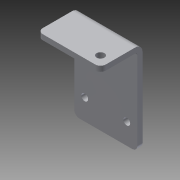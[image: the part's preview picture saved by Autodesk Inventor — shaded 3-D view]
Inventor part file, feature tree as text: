
AUTODESK INVENTOR PART (.ipt)
format: ipt  version: 2014 (Build 180170000, 170)  size: 122,368 bytes
history: native  units: in
note: dims shown in document units (in); Inventor stores cm internally (conversion verified against a paired STEP export)
features: sheet_metal_op x4, sketch x3, other x3, fillet x1
ambient origin geometry x8: Origin, YZ Plane, XZ Plane, XY Plane, X Axis, Y Axis, Z Axis, Center Point
bodies: Solid1 (feature_tree)
feature tree (11):
  sheet_metal_op  "Face1"
  sheet_metal_op  "Flange1"
  fillet  "Fillet1"  Radius=1.5in
  sketch  "Sketch1"  dims[d1=2.0in]
  other  "Plate1"
  sketch  "Sketch2"  dims[d2=0.163in]
  other  "Plate2"
  sheet_metal_op  "Bend1"
  sheet_metal_op  "Corner1"
  sketch  "Sketch4"  dims[d3=0.25in d4=0.7874in d6=1.0in d7=0.3937in d9=1.0in d11=0.125in d12=0.125in d13=0.0625in d14=0.25in d15=0.125in d16=1.0in d17=90.0deg d18=0.05in d19=0.5in d20=0.125in d21=0.125in d22=0.5in d28=0.187in d29=0.25in d30=0.25in d31=0.125in d32=0.0in d33=0.125in]
  other  "Cut2"
